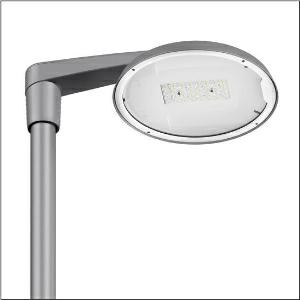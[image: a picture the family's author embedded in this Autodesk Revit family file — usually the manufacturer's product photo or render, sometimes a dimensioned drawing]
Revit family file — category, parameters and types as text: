
# Revit family: dl_r__50_iq_mini___st0_5a_5xa248b31f08je_331a
name_source: partatom
category: Lighting Fixtures
units: mm (PartAtom-declared; Revit-internal decimal feet)

## family parameters
Cut with Voids When Loaded = No
Host = Face
Light Source = No
Part Type = Normal
Room Calculation Point = No
Round Connector Dimension = Use Diameter
Shared = No

## types (1)
- --- (1 x LED, 10300 lm, 66 W, 3000K)
    Apparent Load = 66 VA
    CIE Flux Codes = 43 76 97 100 100
    Color Rendering = 70
    Color Temperature = 3000K
    Default Elevation = 1800 mm
    Description = DL® 50 iQ mini, mast luminaire, primary light control with lens, of PMMA, primary optical cover: cover, of toughened safety glass, transparent, light distribution: ST0.5a, light emission: direct distribution, primary light characteristic: asymmetric, installation type: side-entry, post-top, LED, High Power LED, rated luminous flux: 10.300lm, luminous efficacy: 156lm/W, light colour: 730, colour temperature: 3000K, control: optimised constant luminous flux control (CLO 2.0), Desk-Remote (wireless, voltage-free reading and setting of iQ features in the workshop via application-optimized NFC function/RFID function), Light-Fading, Smart-Wire, Night-Set, Lumen-Switch, Temp-Guard, Auto-Match, Street-Remote, mains connection: 230..240V, AC, 50/60Hz, connection cable pre-assembled, cable length: 8,5m, start of lifetime: 66W, end of service life: 69W, reduction: 30W, luminaire housing, of diecast aluminium, powder-coated, Siteco® metallic grey (DB 702S), inclination adjustable: 0°, 5°, 10° (post-top) | 0°, -5°, -10°, -15° (side-entry), please order mast post-top element or mast side-entry element separately, diameter: 500mm, height: 115mm, post-top: for spigot size d x l = 76 x 100mm; with reducer (optional accessory) 60 x 100mm | side-entry: for spigot size d x l = 60 x 100mm; with reducer (optional accessory) 42 x 100mm, protection rating (complete): IP66, insulation class (complete): insulation class II (safety insulation), certification: CE, ENEC, VDE, impact resistance: IK08, permissible operating ambient temperature for outdoor applications: -25..+40°C, standard-compliant lighting for roads and squares, packaging unit: 1 piece

Light Distribution: ST0.5a
    Height = 115 mm
    Lamp = 1 x LED
    Lamp Light Flux = 10300 lm
    Lamp Power = 66 W
    Lamp count = 1
    Length = 500 mm
    Luminous efficacy = 156 lm/W
    Manufacturer = Siteco
    ModVariant = No
    Model = 5XA248B31F08JE
    Number of Poles = 1
    OnlyDefault = Yes
    Power Factor = 1
    Product Name = DL® 50 iQ mini | ST0.5a
    Product group = mast luminaire | pylon top
    ProductGroupID = 6100
    Protection Class = Protection class II
    Protection Degree = IP 66
    RLX_Detail_Level = 1
    RLX_Emergency_Light_Flux = 0 lm
    RLX_Emergency_Type = 0
    RLX_Emergency_Type_DB = No
    RlxData = <blob elided: 126761 chars, md5=88ebcf37>
    Socket = socket
    Standby Power = 0 W
    System Light Flux = 10300 lm
    System Power = 66 W
    Type Comments = factory setting: luminous flux: 100 % | dim-lin: 254 | 693 mA
    Type Image = l_1251794.jpg
    URL = http://relux.com
    VarID = @adj_092289
    Voltage = 0 V
    Weight = 0.00 kg
    Width = 0 mm  [stored 0 ft]

note: [stored X ft] marks values corroborated as IEEE doubles in the binary element streams (Revit-internal decimal feet)

## geometry (parser evidence)
native form markers: Blend x4, Sweep x12
no freeform markers — native parametric forms only
